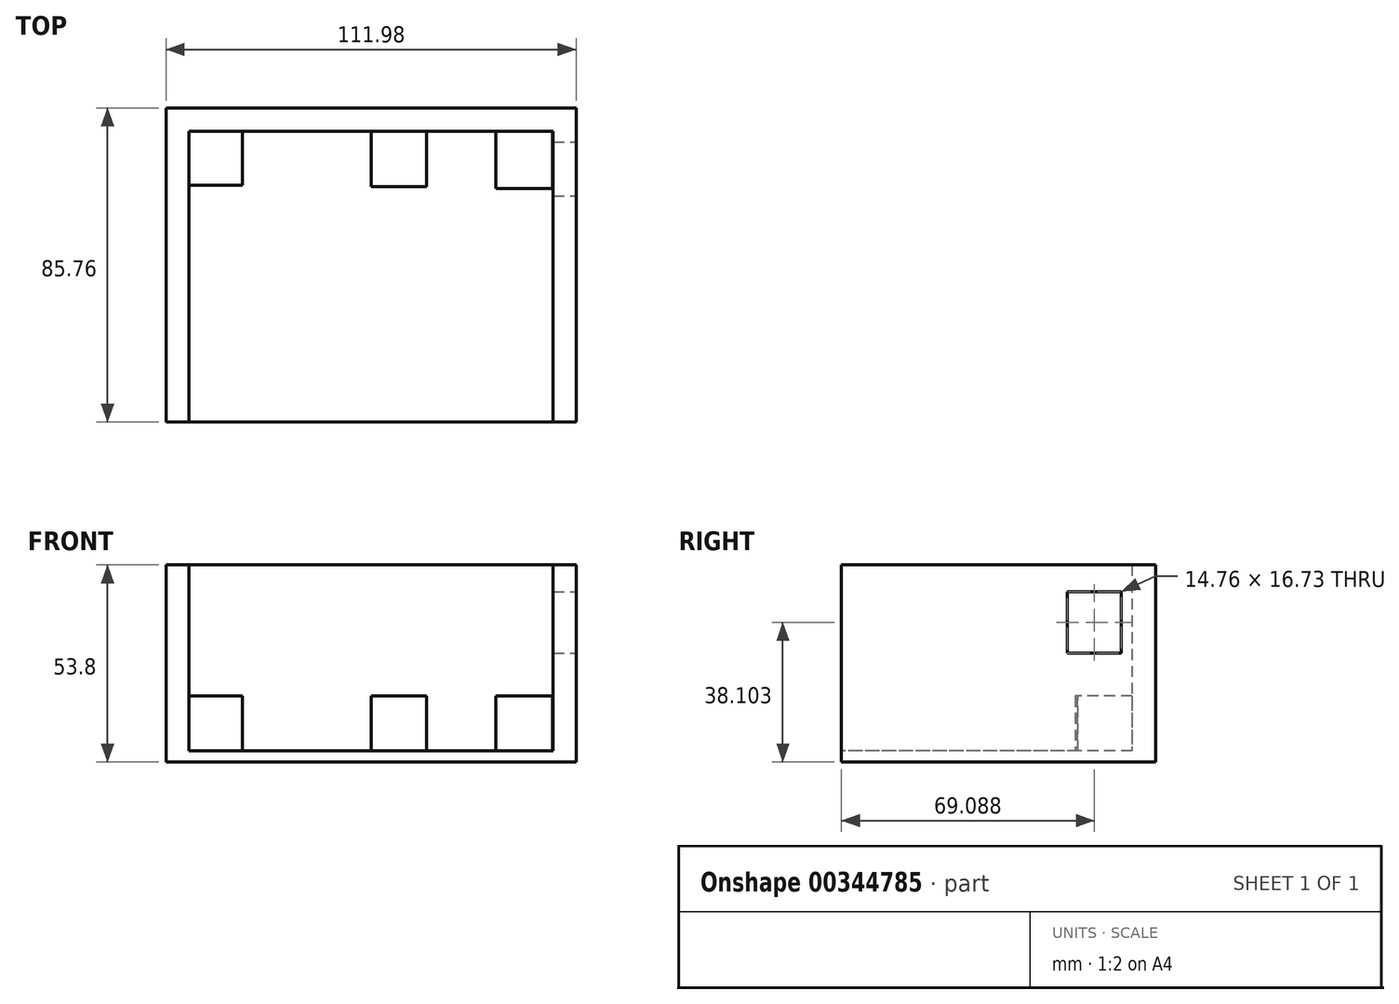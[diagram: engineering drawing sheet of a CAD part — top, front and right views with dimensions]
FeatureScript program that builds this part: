
annotation { "Feature Type Name" : "Feature", "Feature Type Description" : "" }
export const myFeature = defineFeature(function(context is Context, id is Id, definition is map)
    precondition{}
    {
        {
            var Q0;
            Q0=qCreatedBy(makeId("Top.planeOp"),FACE);
            var sketch = newSketch(context, id + "F0", { "sketchPlane" : qUnion([Q0])});
            skLineSegment(sketch, "E0.bottom", {"start": v(56, -42.88) * mm, "end": v(-56, -42.88) * mm});
            skLineSegment(sketch, "E0.top", {"start": v(56, 42.88) * mm, "end": v(-56, 42.88) * mm});
            skLineSegment(sketch, "E0.left", {"start": v(56, -42.88) * mm, "end": v(56, 42.88) * mm});
            skLineSegment(sketch, "E0.right", {"start": v(-56, -42.88) * mm, "end": v(-56, 42.88) * mm});
            skPoint(sketch, "E0.middle", {"position": v(0, 0) * mm});
            skSolve(sketch);
        }
        {
            var Q0;
            Q0=makeQuery(id+"F0.imprint","IMPRINT",FACE,{"disambiguationData":[TD([[makeQuery(id+"F0.imprint","IMPRINT",EDGE,{"derivedFrom":sQuery(id+"F0.wireOp",EDGE,"E0.bottom")}),-1.0]])]});
            extrude(context, id + "F1", {"entities" : qUnion([Q0]), "depth" : 3 * mm});
        }
        {
            var Q0;
            Q0=makeQuery(id+"F1.opExtrude","CAP_FACE",FACE,{"disambiguationData":[OSD([sQuery(id+"F0.wireOp",EDGE,"E0.bottom"),sQuery(id+"F0.wireOp",EDGE,"E0.top"),sQuery(id+"F0.wireOp",EDGE,"E0.left"),sQuery(id+"F0.wireOp",EDGE,"E0.right")])],"isStart":false});
            var sketch = newSketch(context, id + "F2", { "sketchPlane" : qUnion([Q0])});
            skLineSegment(sketch, "E1.bottom", {"start": v(-56, 42.88) * mm, "end": v(-49.71, 42.88) * mm});
            skLineSegment(sketch, "E1.top", {"start": v(-56, -42.88) * mm, "end": v(-49.71, -42.88) * mm});
            skLineSegment(sketch, "E1.left", {"start": v(-56, 42.88) * mm, "end": v(-56, -42.88) * mm});
            skLineSegment(sketch, "E1.right", {"start": v(-49.71, 42.88) * mm, "end": v(-49.71, -42.88) * mm});
            skLineSegment(sketch, "E2.bottom", {"start": v(56, 42.88) * mm, "end": v(49.71, 42.88) * mm});
            skLineSegment(sketch, "E2.top", {"start": v(56, -42.88) * mm, "end": v(49.71, -42.88) * mm});
            skLineSegment(sketch, "E2.left", {"start": v(56, 42.88) * mm, "end": v(56, -42.88) * mm});
            skLineSegment(sketch, "E2.right", {"start": v(49.71, 42.88) * mm, "end": v(49.71, -42.88) * mm});
            skLineSegment(sketch, "E3.bottom", {"start": v(-56, 42.88) * mm, "end": v(56, 42.88) * mm});
            skLineSegment(sketch, "E3.top", {"start": v(-56, 36.48) * mm, "end": v(56, 36.48) * mm});
            skLineSegment(sketch, "E3.left", {"start": v(-56, 42.88) * mm, "end": v(-56, 36.48) * mm});
            skLineSegment(sketch, "E3.right", {"start": v(56, 42.88) * mm, "end": v(56, 36.48) * mm});
            skSolve(sketch);
        }
        {
            var Q0;
            Q0 = qSketchRegion(id + "F2", true);
            extrude(context, id + "F3", {"entities" : qUnion([Q0]), "operationType" : NewBodyOperationType.ADD, "depth" : 50.8 * mm});
        }
        {
            var Q0;
            Q0=makeQuery(id+"F3.boolean.opBoolean","MERGE",FACE,{"derivedFrom":[makeQuery(id+"F1.opExtrude","SWEPT_FACE",FACE,{"disambiguationData":[OSD([sQuery(id+"F0.wireOp",EDGE,"E0.left")])]}),makeQuery(id+"F3.opExtrude","SWEPT_FACE",FACE,{"disambiguationData":[OSD([sQuery(id+"F2.wireOp",EDGE,"E2.left"),sQuery(id+"F2.wireOp",EDGE,"E3.right")])]})]});
            var sketch = newSketch(context, id + "F4", { "sketchPlane" : qUnion([Q0])});
            skLineSegment(sketch, "E4.bottom", {"start": v(33.59, 29.74) * mm, "end": v(18.83, 29.74) * mm});
            skLineSegment(sketch, "E4.top", {"start": v(33.59, 46.47) * mm, "end": v(18.83, 46.47) * mm});
            skLineSegment(sketch, "E4.left", {"start": v(33.59, 29.74) * mm, "end": v(33.59, 46.47) * mm});
            skLineSegment(sketch, "E4.right", {"start": v(18.83, 29.74) * mm, "end": v(18.83, 46.47) * mm});
            skPoint(sketch, "E4.middle", {"position": v(26.2, 38.1) * mm});
            skSolve(sketch);
        }
        {
            var Q0;
            Q0 = qSketchRegion(id + "F4", true);
            extrude(context, id + "F5", {"entities" : qUnion([Q0]), "operationType" : NewBodyOperationType.REMOVE, "oppositeDirection" : true, "depth" : 25.4 * mm});
        }
        {
            var Q0;
            Q0=makeQuery(id+"F1.opExtrude","CAP_FACE",FACE,{"disambiguationData":[OSD([sQuery(id+"F0.wireOp",EDGE,"E0.bottom"),sQuery(id+"F0.wireOp",EDGE,"E0.top"),sQuery(id+"F0.wireOp",EDGE,"E0.left"),sQuery(id+"F0.wireOp",EDGE,"E0.right")])],"isStart":false});
            var sketch = newSketch(context, id + "F6", { "sketchPlane" : qUnion([Q0])});
            skLineSegment(sketch, "E5.bottom", {"start": v(0, 36.48) * mm, "end": v(15.19, 36.48) * mm});
            skLineSegment(sketch, "E5.top", {"start": v(0, 21.41) * mm, "end": v(15.19, 21.41) * mm});
            skLineSegment(sketch, "E5.left", {"start": v(0, 36.48) * mm, "end": v(0, 21.41) * mm});
            skLineSegment(sketch, "E5.right", {"start": v(15.19, 36.48) * mm, "end": v(15.19, 21.41) * mm});
            skSolve(sketch);
        }
        {
            var Q0;
            Q0 = qSketchRegion(id + "F6", true);
            extrude(context, id + "F7", {"entities" : qUnion([Q0]), "operationType" : NewBodyOperationType.ADD, "depth" : 15 * mm});
        }
        {
            var Q0;
            Q0=makeQuery(id+"F1.opExtrude","CAP_FACE",FACE,{"disambiguationData":[OSD([sQuery(id+"F0.wireOp",EDGE,"E0.bottom"),sQuery(id+"F0.wireOp",EDGE,"E0.top"),sQuery(id+"F0.wireOp",EDGE,"E0.left"),sQuery(id+"F0.wireOp",EDGE,"E0.right")])],"isStart":false});
            var sketch = newSketch(context, id + "F8", { "sketchPlane" : qUnion([Q0])});
            skSolve(sketch);
        }
        {
            var Q0;
            {var subQ2=sQuery(id+"F0.wireOp",EDGE,"E0.bottom");Q0=makeQuery(id+"F8.imprint","IMPRINT",FACE,{"disambiguationData":[TD([[makeQuery(id+"F8.imprint","IMPRINT",EDGE,{"derivedFrom":makeQuery(id+"F1.opExtrude","CAP_EDGE",EDGE,{"disambiguationData":[OSD([subQ2])],"isStart":false})}),-1.0]])]});}
            var sketch = newSketch(context, id + "F9", { "sketchPlane" : qUnion([Q0])});
            skLineSegment(sketch, "E6.bottom", {"start": v(-49.8, 36.74) * mm, "end": v(-35.1, 36.74) * mm});
            skLineSegment(sketch, "E6.top", {"start": v(-49.8, 21.77) * mm, "end": v(-35.1, 21.77) * mm});
            skLineSegment(sketch, "E6.left", {"start": v(-49.8, 36.74) * mm, "end": v(-49.8, 21.77) * mm});
            skLineSegment(sketch, "E6.right", {"start": v(-35.1, 36.74) * mm, "end": v(-35.1, 21.77) * mm});
            skLineSegment(sketch, "E7.bottom", {"start": v(49.53, 36.74) * mm, "end": v(34.02, 36.74) * mm});
            skLineSegment(sketch, "E7.top", {"start": v(49.53, 20.96) * mm, "end": v(34.02, 20.96) * mm});
            skLineSegment(sketch, "E7.left", {"start": v(49.53, 36.74) * mm, "end": v(49.53, 20.96) * mm});
            skLineSegment(sketch, "E7.right", {"start": v(34.02, 36.74) * mm, "end": v(34.02, 20.96) * mm});
            skSolve(sketch);
        }
        {
            var Q0;
            Q0 = qSketchRegion(id + "F9", true);
            extrude(context, id + "F10", {"entities" : qUnion([Q0]), "operationType" : NewBodyOperationType.ADD, "depth" : 15 * mm});
        }
    });
